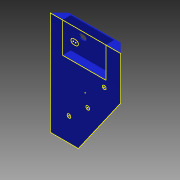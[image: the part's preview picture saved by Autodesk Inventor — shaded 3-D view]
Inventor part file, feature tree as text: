
AUTODESK INVENTOR PART (.ipt)
format: ipt  version: 2015 SP1 (Build 190203100, 203)  size: 184,320 bytes
history: native  units: in
note: dims shown in document units (in); Inventor stores cm internally (conversion verified against a paired STEP export)
features: reference x16, sketch x5, extrude x4, projected_geometry x2, hole x1, plane x1, chamfer x1
ambient origin geometry x8: Origin, YZ Plane, XZ Plane, XY Plane, X Axis, Y Axis, Z Axis, Center Point
bodies: Solid1 (feature_tree)
feature tree (30):
  extrude  "Extrusion1"  Depth=0.5in
  hole  "Hole1"  [1 undecoded]
  plane  "Work Plane1"
  sketch  "Sketch7"  dims[d38=0.201in d39=0.75in d40=0.507in d41=0.25in d42=0.5635in d43=1.0in d44=0.8108in d47=1.0in]
  extrude  "Extrusion7"  Depth=0.7505in
  extrude  "Extrusion9"  Depth=0.4375in
  chamfer  "Chamfer3"  Distance=0.125in
  extrude  "Extrusion10"  Depth=0.4375in
  sketch  "Sketch10"  dims[d65=1.5in d72=0.375in d73=0.125in d74=0.375in d75=0.4375in d76=0.0in d80=1.5in d82=0.4375in d83=0.0in d84=0.3779in d85=0.5in d86=0.125in d87=45.0deg d88=0.133in d89=0.125in d90=0.8in d91=0.7in d92=0.4375in d93=0.0in d108=1.0in d109=2.125in]
  sketch  "Sketch1"  dims[d0=0.5in d1=0.0in d2=3.75in]
  sketch  "Sketch5"  dims[d3=5.5in]
  reference  "Reference22"
  reference  "Reference23"
  reference  "Reference24"
  reference  "Reference25"
  reference  "Reference26"
  reference  "Reference27"
  reference  "Reference28"
  reference  "Reference29"
  reference  "Reference30"
  reference  "Reference31"
  reference  "Reference32"
  reference  "Reference33"
  reference  "Reference34"
  reference  "Reference35"
  reference  "Reference36"
  reference  "Reference37"
  sketch  "Sketch8"  dims[d53=0.875in d64=0.7505in]
  projected_geometry  "Projected Loop1"
  projected_geometry  "Projected Loop2"
note: 1 required parameter value undecoded (feature->parameter linkage not recoverable at this tier; creation-order binding heuristic only, values carry confidence <= 0.55)
